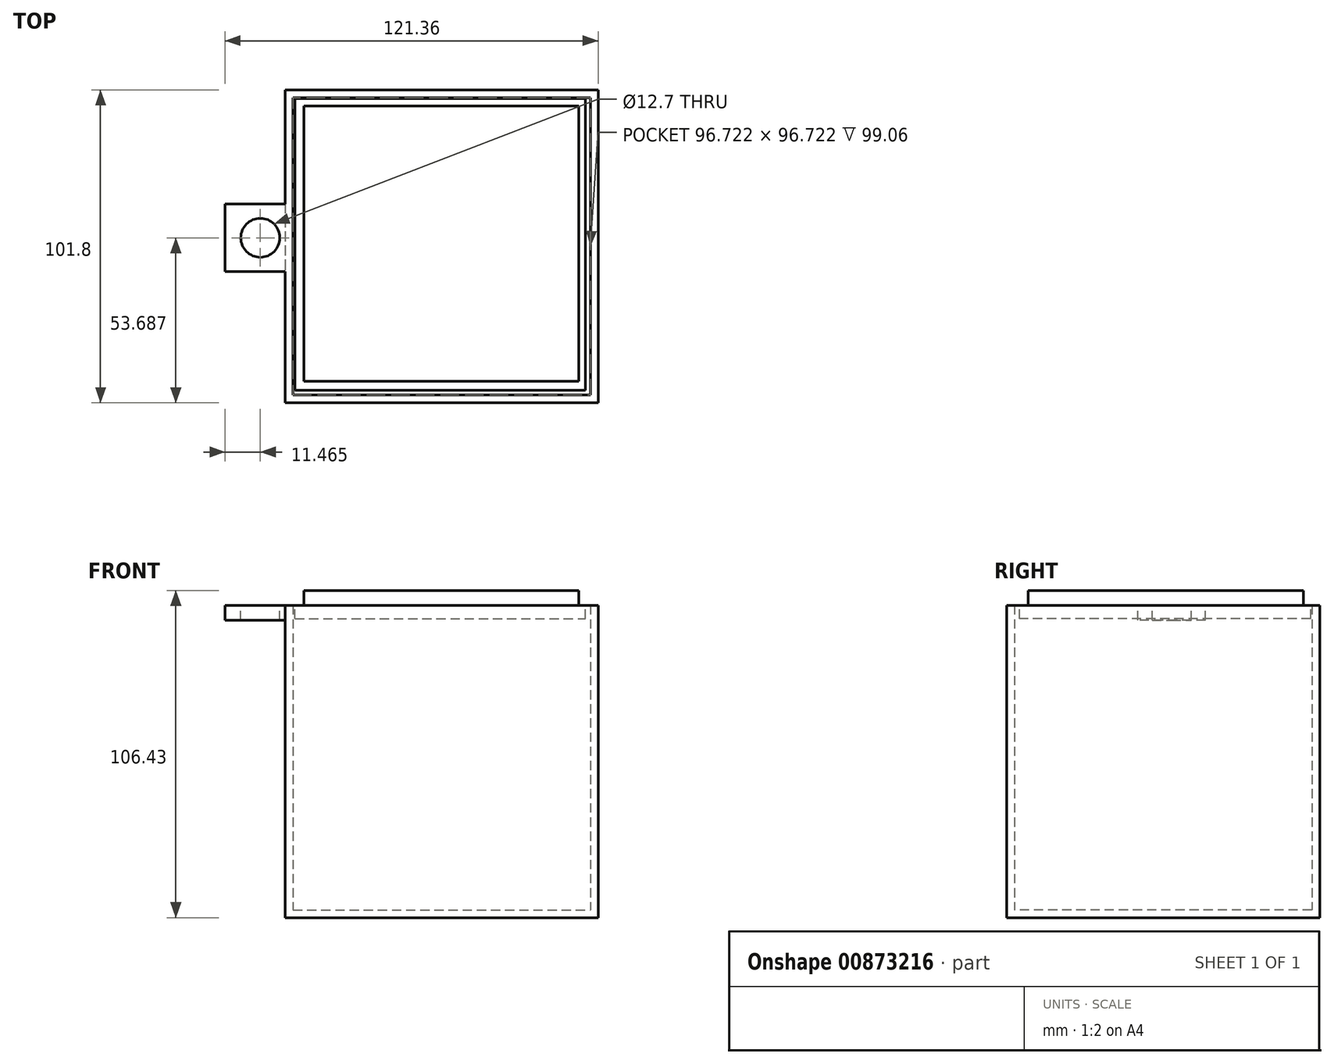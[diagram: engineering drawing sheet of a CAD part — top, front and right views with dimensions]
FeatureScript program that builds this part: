
annotation { "Feature Type Name" : "Feature", "Feature Type Description" : "" }
export const myFeature = defineFeature(function(context is Context, id is Id, definition is map)
    precondition{}
    {
        {
            var Q0;
            Q0=qCreatedBy(makeId("Top.planeOp"),FACE);
            var sketch = newSketch(context, id + "F0", { "sketchPlane" : qUnion([Q0])});
            skLineSegment(sketch, "E0.bottom", {"start": v(-29.75, 33.72) * mm, "end": v(72.06, 33.72) * mm});
            skLineSegment(sketch, "E0.top", {"start": v(-29.75, -68.08) * mm, "end": v(72.06, -68.08) * mm});
            skLineSegment(sketch, "E0.left", {"start": v(-29.75, 33.72) * mm, "end": v(-29.75, -68.08) * mm});
            skLineSegment(sketch, "E0.right", {"start": v(72.06, 33.72) * mm, "end": v(72.06, -68.08) * mm});
            skPoint(sketch, "E1", {"position": v(21.47, -18.45) * mm});
            skSolve(sketch);
        }
        {
            var Q0;
            Q0 = qSketchRegion(id + "F0", true);
            extrude(context, id + "F1", {"entities" : qUnion([Q0]), "depth" : 101.6 * mm, "offsetDistance" : 25.4 * mm});
        }
        {
            var Q0;
            Q0=makeQuery(id+"F1.opExtrude","CAP_FACE",FACE,{"disambiguationData":[OSD([sQuery(id+"F0.wireOp",EDGE,"E0.bottom"),sQuery(id+"F0.wireOp",EDGE,"E0.top"),sQuery(id+"F0.wireOp",EDGE,"E0.left"),sQuery(id+"F0.wireOp",EDGE,"E0.right")])],"isStart":false});
            shell(context, id + "F2", {"entities" : qUnion([Q0]), "thickness" : 2.54 * mm});
        }
        {
            var Q0;
            Q0=makeQuery(id+"F1.opExtrude","CAP_FACE",FACE,{"disambiguationData":[OSD([sQuery(id+"F0.wireOp",EDGE,"E0.bottom"),sQuery(id+"F0.wireOp",EDGE,"E0.top"),sQuery(id+"F0.wireOp",EDGE,"E0.left"),sQuery(id+"F0.wireOp",EDGE,"E0.right")])],"isStart":false});
            var sketch = newSketch(context, id + "F3", { "sketchPlane" : qUnion([Q0])});
            skLineSegment(sketch, "E2.bottom", {"start": v(-26.56, 30.86) * mm, "end": v(67.92, 30.86) * mm});
            skLineSegment(sketch, "E2.top", {"start": v(-26.56, -63.94) * mm, "end": v(67.92, -63.94) * mm});
            skLineSegment(sketch, "E2.left", {"start": v(-26.56, 30.86) * mm, "end": v(-26.56, -63.94) * mm});
            skLineSegment(sketch, "E2.right", {"start": v(67.92, 30.86) * mm, "end": v(67.92, -63.94) * mm});
            skSolve(sketch);
        }
        {
            var Q0;
            Q0 = qSketchRegion(id + "F3", true);
            extrude(context, id + "F4", {"entities" : qUnion([Q0]), "operationType" : NewBodyOperationType.ADD, "oppositeDirection" : true, "depth" : 4.32 * mm, "offsetDistance" : 25.4 * mm});
        }
        {
            var Q0;
            Q0=makeQuery(id+"F3.imprint","IMPRINT",FACE,{"disambiguationData":[TD([[makeQuery(id+"F3.imprint","IMPRINT",EDGE,{"derivedFrom":sQuery(id+"F3.wireOp",EDGE,"E2.bottom")}),-1.0]])]});
            var sketch = newSketch(context, id + "F5", { "sketchPlane" : qUnion([Q0])});
            skLineSegment(sketch, "E3.bottom", {"start": v(-23.62, 28.45) * mm, "end": v(65.75, 28.45) * mm});
            skLineSegment(sketch, "E3.top", {"start": v(-23.62, -61.05) * mm, "end": v(65.75, -61.05) * mm});
            skLineSegment(sketch, "E3.left", {"start": v(-23.62, 28.45) * mm, "end": v(-23.62, -61.05) * mm});
            skLineSegment(sketch, "E3.right", {"start": v(65.75, 28.45) * mm, "end": v(65.75, -61.05) * mm});
            skSolve(sketch);
        }
        {
            var Q0;
            Q0 = qSketchRegion(id + "F5", true);
            extrude(context, id + "F6", {"entities" : qUnion([Q0]), "operationType" : NewBodyOperationType.ADD, "depth" : 4.83 * mm, "offsetDistance" : 25.4 * mm});
        }
        {
            var Q0;
            {var subQ6=sQuery(id+"F0.wireOp",EDGE,"E0.bottom");var subQ7=makeQuery(id+"F1.opExtrude","CAP_EDGE",EDGE,{"disambiguationData":[OSD([subQ6])],"isStart":false});Q0=makeQuery(id+"F3.imprint","IMPRINT",FACE,{"disambiguationData":[TD([[makeQuery(id+"F3.imprint","IMPRINT",EDGE,{"derivedFrom":subQ7}),-1.0]])]});}
            var sketch = newSketch(context, id + "F7", { "sketchPlane" : qUnion([Q0])});
            skLineSegment(sketch, "E4.bottom", {"start": v(-28.34, -3.4) * mm, "end": v(-49.3, -3.4) * mm});
            skLineSegment(sketch, "E4.top", {"start": v(-28.34, -25.38) * mm, "end": v(-49.3, -25.38) * mm});
            skLineSegment(sketch, "E4.left", {"start": v(-28.34, -3.4) * mm, "end": v(-28.34, -25.38) * mm});
            skLineSegment(sketch, "E4.right", {"start": v(-49.3, -3.4) * mm, "end": v(-49.3, -25.38) * mm});
            skPoint(sketch, "E5", {"position": v(-37.84, -14.4) * mm});
            skPoint(sketch, "E5.positionSnap0", {"position": v(-49.3, -14.4) * mm});
            skSolve(sketch);
        }
        {
            var Q0;
            Q0 = qSketchRegion(id + "F7", true);
            extrude(context, id + "F8", {"entities" : qUnion([Q0]), "operationType" : NewBodyOperationType.ADD, "oppositeDirection" : true, "depth" : 4.83 * mm, "offsetDistance" : 25.4 * mm});
        }
        {
            var Q0;
            Q0=sQuery(id+"F7.wireOp",VERTEX,"E5");
            var Q1;
            Q1=makeQuery(id+"F1.opExtrude","SWEPT_BODY",BODY,{"disambiguationData":[OSD([sQuery(id+"F0.wireOp",EDGE,"E0.bottom"),sQuery(id+"F0.wireOp",EDGE,"E0.top"),sQuery(id+"F0.wireOp",EDGE,"E0.left"),sQuery(id+"F0.wireOp",EDGE,"E0.right")])]});
            hole(context, id + "F9", {"style" : HoleStyle.SIMPLE, "endStyle" : HoleEndStyle.THROUGH, "holeDiameter" : 12.7 * mm, "majorDiameter" : 6.35 * mm, "isTappedThrough" : true, "tappedDepth" : 12.7 * mm, "tapClearance" : 3, "locations" : qUnion([Q0]), "scope" : qUnion([Q1])});
        }
    });
